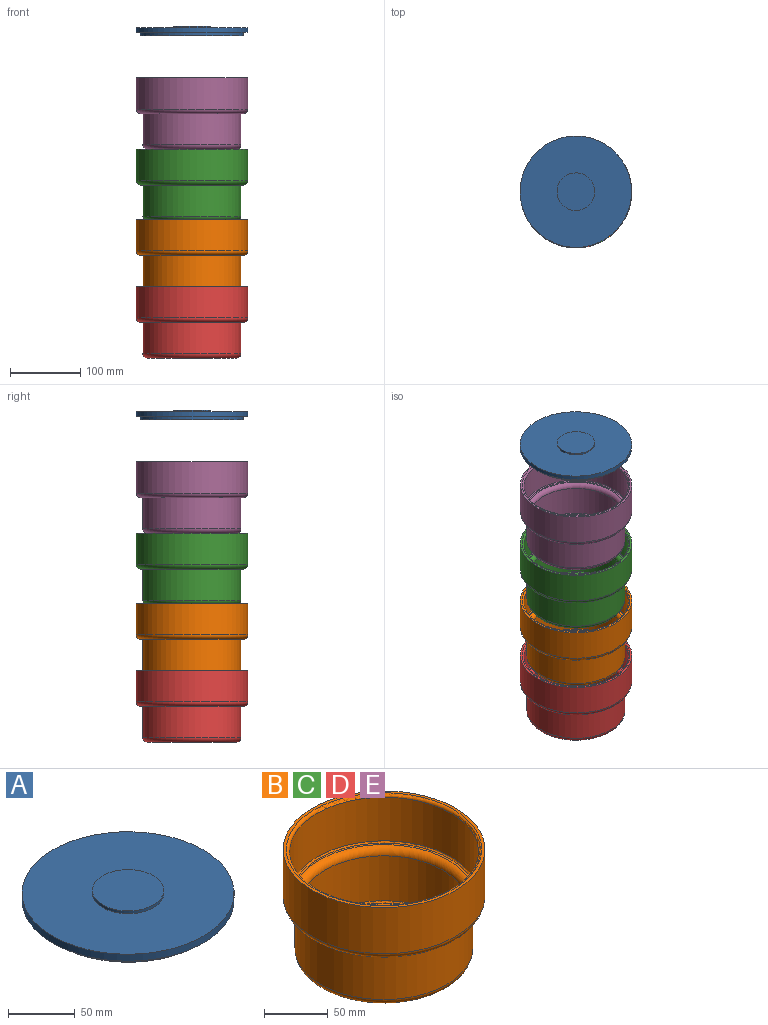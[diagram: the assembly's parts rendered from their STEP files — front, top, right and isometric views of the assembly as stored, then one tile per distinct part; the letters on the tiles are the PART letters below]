
ASSEMBLY  parts=5 mates=4
PART A: 7 faces, bbox 158.6x158.6x14 mm
  f0: cylinder r=79.31mm len=158.63mm, axis (0,0,-1), area 3164.5mm2, adj f1,f2
  f1: plane 158.63x158.63mm, normal (0,0,1), area 17511.1mm2, adj f0,f5
  f2: plane 158.63x158.63mm, normal (0,0,-1), area 2834.7mm2, adj f0,f3
  f3: cylinder r=73.41mm len=146.81mm, axis (0,0,1), area 2343mm2, adj f2,f4
  f4: plane 146.81x146.81mm, normal (0,0,-1), area 16928mm2, adj f3
  f5: cylinder r=26.77mm len=53.54mm, axis (0,0,-1), area 427.2mm2, adj f1,f6
  f6: plane 53.54x53.54mm, normal (0,0,1), area 2251.6mm2, adj f5
PART B: 17 faces, bbox 171.8x171.8x101.6 mm
  f0: cylinder r=69.85mm len=139.7mm, axis (0,0,-1), area 19508.2mm2, adj f4,f6
  f1: plane 127x127mm, normal (0,0,-1), area 10290.1mm2, adj f6,f15
  f2: cylinder r=79.38mm len=158.75mm, axis (0,0,-1), area 22168.5mm2, adj f3,f5
  f3: plane 158.75x158.75mm, normal (0,0,1), area 1246.5mm2, adj f2,f14
  f4: plane 146.05x146.05mm, normal (0,0,-1), area 1425.1mm2, adj f0,f5
  f5: torus R=73.03mm, axis (0,0,1), area 4830mm2, adj f2,f4
  f6: torus R=63.5mm, axis (0,0,1), area 4233mm2, adj f0,f1
  f7: cylinder r=64.77mm len=129.54mm, axis (0,0,-1), area 17572.6mm2, adj f12,f13
  f8: plane 127x127mm, normal (0,0,1), area 12667.7mm2, adj f12
  f9: cylinder r=74.3mm len=148.59mm, axis (0,0,-1), area 19564mm2, adj f11,f14
  f10: plane 146.05x146.05mm, normal (0,0,1), area 862.7mm2, adj f11,f13
  f11: torus R=73.03mm, axis (0,0,1), area 925.5mm2, adj f9,f10
  f12: torus R=63.5mm, axis (0,0,1), area 806.1mm2, adj f7,f8
  f13: torus R=71.12mm, axis (0,0,1), area 4203.9mm2, adj f7,f10
  f14: torus R=76.83mm, axis (0,0,1), area 1885.6mm2, adj f3,f9
  f15: cylinder r=27.51mm len=55.02mm, axis (0,0,-1), area 439mm2, adj f1,f16
  f16: plane 55.02x55.02mm, normal (0,0,-1), area 2377.6mm2, adj f15
PART C: same geometry as B
PART D: same geometry as B
PART E: same geometry as B
PLACE A t=(60.59,-123.42,268.5)mm
PLACE B t=(60.81,-123.49,1.77)mm
PLACE C t=(60.81,-123.49,101.8)mm
PLACE D t=(60.81,-123.49,-93.64)mm
PLACE E t=(60.81,-123.49,203.56)mm
MATE cylindrical D.f0 <-> A.f0  axis (0,0,-1) through (60.59,-123.42,-65.07)mm
MATE cylindrical D.f2 <-> C.f2  axis (0,0,-1) through (60.81,-123.49,-15.54)mm
MATE cylindrical D.f2 <-> B.f2  axis (0,0,-1) through (60.81,-123.49,-14.27)mm
MATE cylindrical D.f2 <-> E.f2  axis (0,0,-1) through (60.81,-123.49,-14.27)mm
